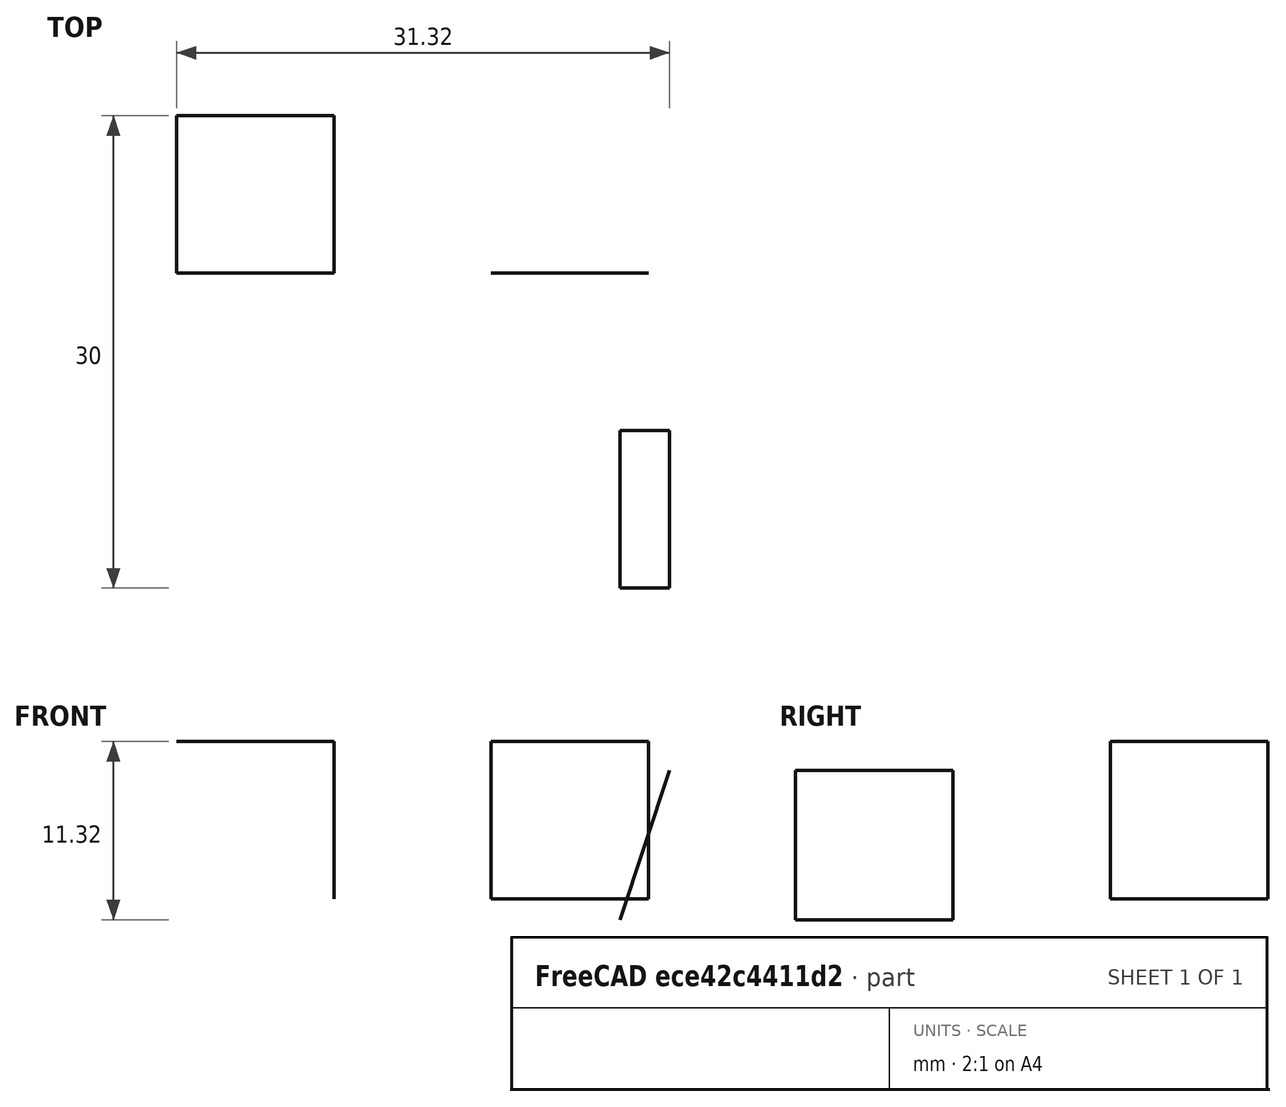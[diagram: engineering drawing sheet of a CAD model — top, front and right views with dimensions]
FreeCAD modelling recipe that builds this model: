
FCSTD DOCUMENT  (FreeCAD 0.19R17089 +1543 (Git))
Label: rt-super-c
License: All rights reserved
LicenseURL: http://en.wikipedia.org/wiki/All_rights_reserved
objects: App::FeaturePython×13, Part::FeaturePython×9, App::LinkElement×4, App::Link×1
note: 8 computed .brp shape members not serialized (recipe doc carries the construction recipe); baked Part::Feature solids carry a one-line shape summary decoded from their .brp
EXTERNAL_REF file=rt-super-a.FCStd obj=Assembly

FEATURE [App::LinkElement] Link_i0
  LinkPlacement = pos=(16,-1.127e-13,5) rot=(2e-06,-1,0;0rad)
  LinkedObject = -> <external rt-super-a.FCStd>#Assembly
  Placement = pos=(16,-1.127e-13,5) rot=(2e-06,-1,0;0rad)
FEATURE [App::LinkElement] Link_i1
  LinkPlacement = pos=(31,1.0311e-12,1.44746e-06) rot=(0.57735,-0.57735,-0.57735;2.0944rad)
  LinkedObject = -> <external rt-super-a.FCStd>#Assembly
  Placement = pos=(31,1.0311e-12,1.44746e-06) rot=(0.57735,-0.57735,-0.57735;2.0944rad)
FEATURE [App::LinkElement] Link_i2
  LinkPlacement = pos=(36,-15,2.55364e-07) rot=(0.974833,-0.157641,-0.157641;4.6869rad)
  LinkedObject = -> <external rt-super-a.FCStd>#Assembly
  Placement = pos=(36,-15,2.55364e-07) rot=(0.974833,-0.157641,-0.157641;4.6869rad)
FEATURE [App::LinkElement] Link_i3
  LinkPlacement = pos=(50.2355,-20,-4.7277) rot=(0,1,0;5.03303rad)
  LinkedObject = -> <external rt-super-a.FCStd>#Assembly
  Placement = pos=(50.2355,-20,-4.7277) rot=(0,1,0;5.03303rad)
FEATURE [App::Link] Link  label="Assembly"
  ElementCount = 4
  ElementList = -> [Link_i0,Link_i1,Link_i2,Link_i3]
  LinkedObject = -> <external rt-super-a.FCStd>#Assembly
FEATURE [Part::FeaturePython] Parts  # WARN: FeaturePython — macro-defined, semantics opaque (R4)
  Group = -> [Link]
  GroupMode = 0
FEATURE [Part::FeaturePython] Assembly  label="Assembly001"  # WARN: FeaturePython — macro-defined, semantics opaque (R4)
  AutoRelax = true
  BuildShape = 0
  Freeze = false
  Group = -> [Constraints,Elements,Parts]
  GroupMode = 1
  SolverType = 1
  Verbose = false
  _SolverType = 1
  _Version = 1
FEATURE [App::FeaturePython] Constraints  # WARN: FeaturePython — macro-defined, semantics opaque (R4)
  Group = -> [Constraint,Constraint001,Constraint002,Constraint003]
  GroupMode = 1
  _Version = 1
FEATURE [App::FeaturePython] Elements  # WARN: FeaturePython — macro-defined, semantics opaque (R4)
  Group = -> [_Element,_Element001,_Element002,_Element003,_Element004,_Element005,_Element007]
  GroupMode = 1
FEATURE [App::FeaturePython] Constraint  label="PlaneCoincident"  # WARN: FeaturePython — macro-defined, semantics opaque (R4)
  Angle = 0
  AnglePitch = 0
  AngleRoll = 0
  Cascade = false
  ConstraintType = 2
  Disabled = false
  Group = -> [ElementLink,ElementLink001]
  GroupMode = 1
  LockAngle = false
  Multiply = false
  OffsetX = 0
  OffsetY = 0
  _ConstraintType = 35
  _Parent = -> Constraints
FEATURE [App::FeaturePython] ElementLink  label="_Element"  # link proxy (typed FeaturePython)
  LinkTransform = true
  LinkedObject = -> _Element
  _Parent = -> Constraint
FEATURE [Part::FeaturePython] _Element  # link proxy (typed FeaturePython)
  Detach = false
  LinkTransform = true
  LinkedObject = -> Link [Link_i1.1.$Cylinder Top.]
  _Parent = -> Elements
FEATURE [App::FeaturePython] ElementLink001  label="_Element001"  # link proxy (typed FeaturePython)
  LinkTransform = true
  LinkedObject = -> _Element001
  _Parent = -> Constraint
FEATURE [Part::FeaturePython] _Element001  # link proxy (typed FeaturePython)
  Detach = false
  LinkTransform = true
  LinkedObject = -> Link [Link_i0.1.$Base Right.]
  _Parent = -> Elements
FEATURE [App::FeaturePython] Constraint001  label="PlaneCoincident001"  # WARN: FeaturePython — macro-defined, semantics opaque (R4)
  Angle = 0
  AnglePitch = 0
  AngleRoll = 0
  Cascade = false
  ConstraintType = 2
  Disabled = false
  Group = -> [ElementLink002,ElementLink003]
  GroupMode = 1
  LockAngle = false
  Multiply = false
  OffsetX = 0
  OffsetY = 0
  _ConstraintType = 35
  _Parent = -> Constraints
FEATURE [App::FeaturePython] ElementLink002  label="_Element002"  # link proxy (typed FeaturePython)
  LinkTransform = true
  LinkedObject = -> _Element002
  _Parent = -> Constraint001
FEATURE [Part::FeaturePython] _Element002  # link proxy (typed FeaturePython)
  Detach = false
  LinkTransform = true
  LinkedObject = -> Link [Link_i2.1.$Cylinder Top.]
  _Parent = -> Elements
FEATURE [App::FeaturePython] ElementLink003  label="_Element003"  # link proxy (typed FeaturePython)
  LinkTransform = true
  LinkedObject = -> _Element003
  _Parent = -> Constraint001
FEATURE [Part::FeaturePython] _Element003  # link proxy (typed FeaturePython)
  Detach = false
  LinkTransform = true
  LinkedObject = -> Link [Link_i1.1.$Base Right.]
  _Parent = -> Elements
FEATURE [App::FeaturePython] Constraint002  label="PlaneCoincident002"  # WARN: FeaturePython — macro-defined, semantics opaque (R4)
  Angle = 0
  AnglePitch = 0
  AngleRoll = 0
  Cascade = false
  ConstraintType = 2
  Disabled = false
  Group = -> [ElementLink004,ElementLink005]
  GroupMode = 1
  LockAngle = false
  Multiply = false
  OffsetX = 0
  OffsetY = 0
  _ConstraintType = 35
  _Parent = -> Constraints
FEATURE [App::FeaturePython] ElementLink004  label="_Element004"  # link proxy (typed FeaturePython)
  LinkTransform = true
  LinkedObject = -> _Element004
  _Parent = -> Constraint002
FEATURE [Part::FeaturePython] _Element004  # link proxy (typed FeaturePython)
  Detach = false
  LinkTransform = true
  LinkedObject = -> Link [Link_i3.1.$Cylinder Top.]
  _Parent = -> Elements
FEATURE [App::FeaturePython] ElementLink005  label="_Element005"  # link proxy (typed FeaturePython)
  LinkTransform = true
  LinkedObject = -> _Element005
  _Parent = -> Constraint002
FEATURE [Part::FeaturePython] _Element005  # link proxy (typed FeaturePython)
  Detach = false
  LinkTransform = true
  LinkedObject = -> Link [Link_i2.1.$Base Right.]
  _Parent = -> Elements
FEATURE [App::FeaturePython] Constraint003  label="Locked"  # WARN: FeaturePython — macro-defined, semantics opaque (R4)
  ConstraintType = 0
  Disabled = false
  Group = -> [ElementLink006]
  GroupMode = 1
  _ConstraintType = 0
  _Parent = -> Constraints
FEATURE [App::FeaturePython] ElementLink006  label="_Element008"  # link proxy (typed FeaturePython)
  LinkTransform = true
  LinkedObject = -> _Element007
  _Parent = -> Constraint003
FEATURE [Part::FeaturePython] _Element007  label="_Element008"  # link proxy (typed FeaturePython)
  Detach = false
  LinkTransform = true
  LinkedObject = -> Link [Link_i0.1.$Base Top.]
  _Parent = -> Elements

RESOLVED EXTERNAL PARTS (link-assembly join: the EXTERNAL_REF files above that resolve inside this repo's crawl, each included once):
---- part rt-super-a.FCStd = doc fcstd_b6c9d386269d ----
FCSTD DOCUMENT  (FreeCAD 0.19R17089 +1543 (Git))
Label: rt-super-a
License: All rights reserved
LicenseURL: http://en.wikipedia.org/wiki/All_rights_reserved
objects: Part::FeaturePython×7, App::FeaturePython×5, Sketcher::SketchObject×2, PartDesign::Pad×2, PartDesign::Body×2
note: 14 computed .brp shape members not serialized (recipe doc carries the construction recipe); baked Part::Feature solids carry a one-line shape summary decoded from their .brp

FEATURE [Sketcher::SketchObject] Sketch
  MapMode = 5
  Support = -> [XY_Plane]
  sketch-geometry (5):
    g0: LineSegment StartX=5 StartY=5 StartZ=0 EndX=-5 EndY=5 EndZ=0
    g1: LineSegment StartX=-5 StartY=5 StartZ=0 EndX=-5 EndY=-5 EndZ=0
    g2: LineSegment StartX=-5 StartY=-5 StartZ=0 EndX=5 EndY=-5 EndZ=0
    g3: LineSegment StartX=5 StartY=-5 StartZ=0 EndX=5 EndY=5 EndZ=0
    g4: Circle [constr] CenterX=0 CenterY=0 CenterZ=0 NormalX=0 NormalY=0 NormalZ=1 AngleXU=0 Radius=7.07107
  constraints (14):
    c: Coincident(g0,g1)
    c: Coincident(g1,g2)
    c: Coincident(g2,g3)
    c: Coincident(g3,g0)
    c: Equal(g0,g1)
    c: Equal(g0,g2)
    c: Equal(g0,g3)
    c: PointOnObject(g0,g4)
    c: PointOnObject(g1,g4)
    c: PointOnObject(g2,g4)
    c: PointOnObject(g3,g4)
    c: Coincident(g4,g-1)
    c: Horizontal(g0)
    c: Distance(g2) = 10
FEATURE [PartDesign::Pad] Pad
  ClaimChildren = false
  Length = 10
  Length2 = 100
  Profile = -> Sketch
  Type = 0
FEATURE [PartDesign::Body] Body
  Group = -> [Sketch,Pad]
  Origin = -> Origin
  Placement = pos=(0,0,-10) rot=(0,0,1;0rad)
  Tip = -> Pad
FEATURE [Sketcher::SketchObject] Sketch001
  MapMode = 5
  Support = -> [XY_Plane001]
  sketch-geometry (1):
    g0: Circle CenterX=0 CenterY=0 CenterZ=0 NormalX=0 NormalY=0 NormalZ=1 AngleXU=0 Radius=2.5
  constraints (2):
    c: Coincident(g0,g-1)
    c: Diameter(g0) = 5
FEATURE [PartDesign::Pad] Pad001
  ClaimChildren = false
  Length = 10
  Length2 = 100
  Profile = -> Sketch001
  Type = 0
FEATURE [PartDesign::Body] Body001
  Group = -> [Sketch001,Pad001]
  Origin = -> Origin001
  Tip = -> Pad001
FEATURE [Part::FeaturePython] Parts  # WARN: FeaturePython — macro-defined, semantics opaque (R4)
  Group = -> [Body,Body001]
  GroupMode = 0
FEATURE [Part::FeaturePython] Assembly  # WARN: FeaturePython — macro-defined, semantics opaque (R4)
  AutoRelax = true
  BuildShape = 0
  Freeze = false
  Group = -> [Constraints,Elements,Parts]
  GroupMode = 1
  SolverType = 1
  Verbose = false
  _SolverType = 1
  _Version = 1
FEATURE [App::FeaturePython] Constraints  # WARN: FeaturePython — macro-defined, semantics opaque (R4)
  Group = -> [Constraint]
  GroupMode = 1
  _Version = 1
FEATURE [App::FeaturePython] Elements  # WARN: FeaturePython — macro-defined, semantics opaque (R4)
  Group = -> [Element,Element001,Element002,Element003,Element004]
  GroupMode = 1
FEATURE [Part::FeaturePython] Element  label="Cylinder Top"  # link proxy (typed FeaturePython)
  Detach = false
  LinkTransform = true
  LinkedObject = -> Body001 [Pad001.Edge3]
  _Parent = -> Elements
FEATURE [Part::FeaturePython] Element001  label="Cylinder Bottom"  # link proxy (typed FeaturePython)
  Detach = false
  LinkTransform = true
  LinkedObject = -> Body001 [Pad001.Edge2]
  _Parent = -> Elements
FEATURE [Part::FeaturePython] Element002  label="Base Top"  # link proxy (typed FeaturePython)
  Detach = false
  LinkTransform = true
  LinkedObject = -> Body [Pad.Face6]
  _Parent = -> Elements
FEATURE [Part::FeaturePython] Element003  label="Base Right"  # link proxy (typed FeaturePython)
  Detach = false
  LinkTransform = true
  LinkedObject = -> Body [Pad.Face4]
  _Parent = -> Elements
FEATURE [App::FeaturePython] Constraint  label="PlaneCoincident"  # WARN: FeaturePython — macro-defined, semantics opaque (R4)
  Angle = 0
  AnglePitch = 0
  AngleRoll = 0
  Cascade = false
  ConstraintType = 2
  Disabled = false
  Group = -> [ElementLink,ElementLink001]
  GroupMode = 1
  LockAngle = false
  Multiply = false
  OffsetX = 0
  OffsetY = 0
  _ConstraintType = 35
  _Parent = -> Constraints
FEATURE [App::FeaturePython] ElementLink  label="Cylinder Bottom"  # link proxy (typed FeaturePython)
  LinkTransform = true
  LinkedObject = -> Element001
  _Parent = -> Constraint
FEATURE [App::FeaturePython] ElementLink001  label="Base Top"  # link proxy (typed FeaturePython)
  LinkTransform = true
  LinkedObject = -> Element002
  _Parent = -> Constraint
FEATURE [Part::FeaturePython] Element004  # link proxy (typed FeaturePython)
  Detach = false
  LinkTransform = true
  LinkedObject = -> Body [Pad.Face3]
  _Parent = -> Elements
